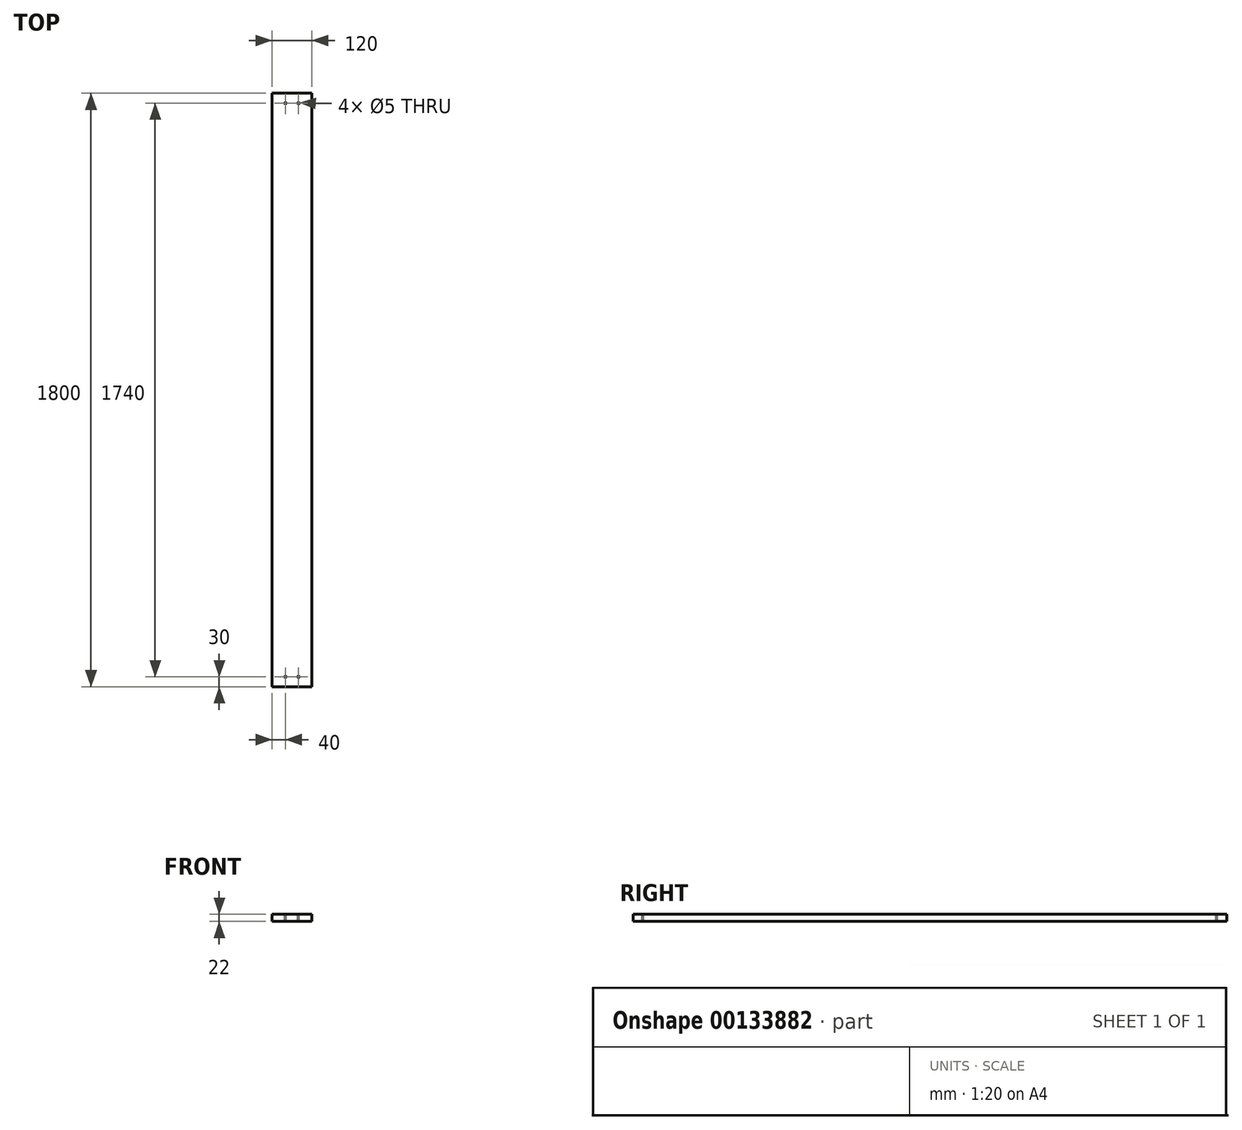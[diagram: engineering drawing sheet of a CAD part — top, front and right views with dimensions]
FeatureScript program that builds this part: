
annotation { "Feature Type Name" : "Feature", "Feature Type Description" : "" }
export const myFeature = defineFeature(function(context is Context, id is Id, definition is map)
    precondition{}
    {
        {
            assignVariable(context, id + "F0", {"name" : "Staerke", "anyValue" : 22 * mm});
        }
        {
            var Q0;
            Q0=qCreatedBy(makeId("Top.planeOp"),FACE);
            var sketch = newSketch(context, id + "F1", { "sketchPlane" : qUnion([Q0])});
            skLineSegment(sketch, "E0.bottom", {"start": v(-60, 1800) * mm, "end": v(60, 1800) * mm});
            skLineSegment(sketch, "E0.top", {"start": v(-60, 0) * mm, "end": v(60, 0) * mm});
            skLineSegment(sketch, "E0.left", {"start": v(-60, 1800) * mm, "end": v(-60, 0) * mm});
            skLineSegment(sketch, "E0.right", {"start": v(60, 1800) * mm, "end": v(60, 0) * mm});
            skSolve(sketch);
        }
        {
            var Q0;
            Q0=makeQuery(id+"F1.imprint","IMPRINT",FACE,{"disambiguationData":[TD([[makeQuery(id+"F1.imprint","IMPRINT",EDGE,{"derivedFrom":sQuery(id+"F1.wireOp",EDGE,"E0.bottom")}),-1.0]])]});
            extrude(context, id + "F2", {"entities" : qUnion([Q0]), "depth" : getVariable(context, 'Staerke')});
        }
        {
            var Q0;
            Q0=makeQuery(id+"F2.opExtrude","CAP_FACE",FACE,{"disambiguationData":[OSD([sQuery(id+"F1.wireOp",EDGE,"E0.bottom"),sQuery(id+"F1.wireOp",EDGE,"E0.top"),sQuery(id+"F1.wireOp",EDGE,"E0.left"),sQuery(id+"F1.wireOp",EDGE,"E0.right")])],"isStart":false});
            var sketch = newSketch(context, id + "F3", { "sketchPlane" : qUnion([Q0])});
            skPoint(sketch, "E1", {"position": v(-20, 30) * mm});
            skPoint(sketch, "E2", {"position": v(20, 30) * mm});
            skLineSegment(sketch, "E3", {"start": v(-60, 30) * mm, "end": v(60, 30) * mm, "construction": true});
            skLineSegment(sketch, "E4", {"start": v(-60, 900) * mm, "end": v(60, 900) * mm, "construction": true});
            skLineSegment(sketch, "E5.MirrorCS", {"start": v(-60, 1770) * mm, "end": v(60, 1770) * mm, "construction": true});
            skPoint(sketch, "E6.MirrorP", {"position": v(-20, 1770) * mm});
            skPoint(sketch, "E7.MirrorP", {"position": v(20, 1770) * mm});
            skSolve(sketch);
        }
        {
            var Q0;
            Q0=sQuery(id+"F3.wireOp",VERTEX,"E6.MirrorP");
            var Q1;
            Q1=sQuery(id+"F3.wireOp",VERTEX,"E7.MirrorP");
            var Q2;
            Q2=sQuery(id+"F3.wireOp",VERTEX,"E1");
            var Q3;
            Q3=sQuery(id+"F3.wireOp",VERTEX,"E2");
            var Q4;
            Q4=makeQuery(id+"F2.opExtrude","SWEPT_BODY",BODY,{"disambiguationData":[OSD([sQuery(id+"F1.wireOp",EDGE,"E0.bottom"),sQuery(id+"F1.wireOp",EDGE,"E0.top"),sQuery(id+"F1.wireOp",EDGE,"E0.left"),sQuery(id+"F1.wireOp",EDGE,"E0.right")])]});
            hole(context, id + "F4", {"style" : HoleStyle.SIMPLE, "endStyle" : HoleEndStyle.THROUGH, "holeDiameter" : 5 * mm, "startFromSketch" : true, "locations" : qUnion([Q0, Q1, Q2, Q3]), "scope" : qUnion([Q4]), "isTappedThrough" : true});
        }
    });
